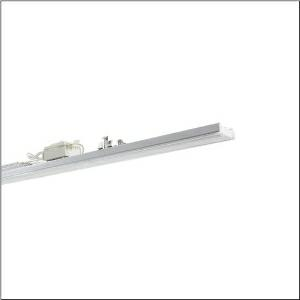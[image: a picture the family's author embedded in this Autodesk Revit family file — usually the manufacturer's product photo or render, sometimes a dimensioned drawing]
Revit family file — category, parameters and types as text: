
# Revit family: licross_r__21_recessed_mo_52tl11dn68xg_a339
name_source: partatom
category: Lighting Fixtures
units: mm (PartAtom-declared; Revit-internal decimal feet)

## family parameters
Cut with Voids When Loaded = No
Host = Face
Light Source = No
Part Type = Normal
Room Calculation Point = No
Round Connector Dimension = Use Diameter
Shared = No

## types (1)
- --- (1 x LED, 8000 lm, 46.3 W, 6500K)
    Apparent Load = 46 VA
    CIE Flux Codes = 89 96 99 100 100
    Color Rendering = 80
    Color Temperature = 6500K
    Default Elevation = 1800 mm
    Description = Licross® 21 Recessed MO, luminaire insert, of sheet steel, galvanised, coil coated, white, length: 1.500mm, width: 66mm, height: 67mm, LED rated luminous flux: 8.000lm, light colour: 865, control gear: DALI 2, with plug, 5-pole, with phase selection, mains connection: 220..240V, AC, 50/60Hz, rated input power: 46W, internal wiring halogen-free, primary light control with lens, of plastic, primary optical cover: cover, of PMMA, light emission: direct distribution, primary light characteristic: symmetric, protection rating (complete): IP40, insulation class (complete): insulation class I (protective earthing), certification: CE, ENEC, VDE, UKCA, protection symbol: D if used in an environment without relevant dust loads with corresponding accessories, impact resistance: IK06, permissible ambient temperature for indoor applications: -25..+40°C, corresponds to IFS (International Featured Standards) requirements for safety and quality in the food industry, reducing of maximum allowable ambient temperature of 5°C with ceiling mounting, LABS conformity tested according to VDMA 24364:2018-05, packaging unit: 1 piece
    Height = 58 mm
    Lamp = 1 x LED
    Lamp Light Flux = 8000 lm
    Lamp Power = 46.3 W
    Lamp count = 1
    Length = 1500 mm
    Luminous efficacy = 173 lm/W
    Manufacturer = Siteco
    ModVariant = No
    Model = 52TL11DN68XG
    Mounting Place = Ceiling
    Mounting Type = Pendant
    Number of Poles = 1
    OnlyDefault = Yes
    Power Factor = 1
    Product Name = Licross® 21 Recessed MO
    Product group = luminaire insert | ceiling pendant
    ProductGroupID = 902
    Protection Class = Protection class I
    Protection Degree = IP 40
    RLX_Detail_Level = 1
    RLX_Emergency_Light_Flux = 0 lm
    RLX_Emergency_Type = 0
    RLX_Emergency_Type_DB = No
    RlxData = <blob elided: 24553 chars, md5=afcc9a2f>
    Socket = socket
    Standby Power = 0 W
    System Light Flux = 8000 lm
    System Power = 46 W
    Type Comments = factory setting: luminous flux: 100 % | dim-lin: 254 | 311 mA
    Type Image = l_1296930.jpg
    URL = http://relux.com
    VarID = @adj_030237
    Voltage = 0 V
    Weight = 0.00 kg
    Width = 66 mm

## geometry (parser evidence)
native form markers: Blend x4, Sweep x12
no freeform markers — native parametric forms only
